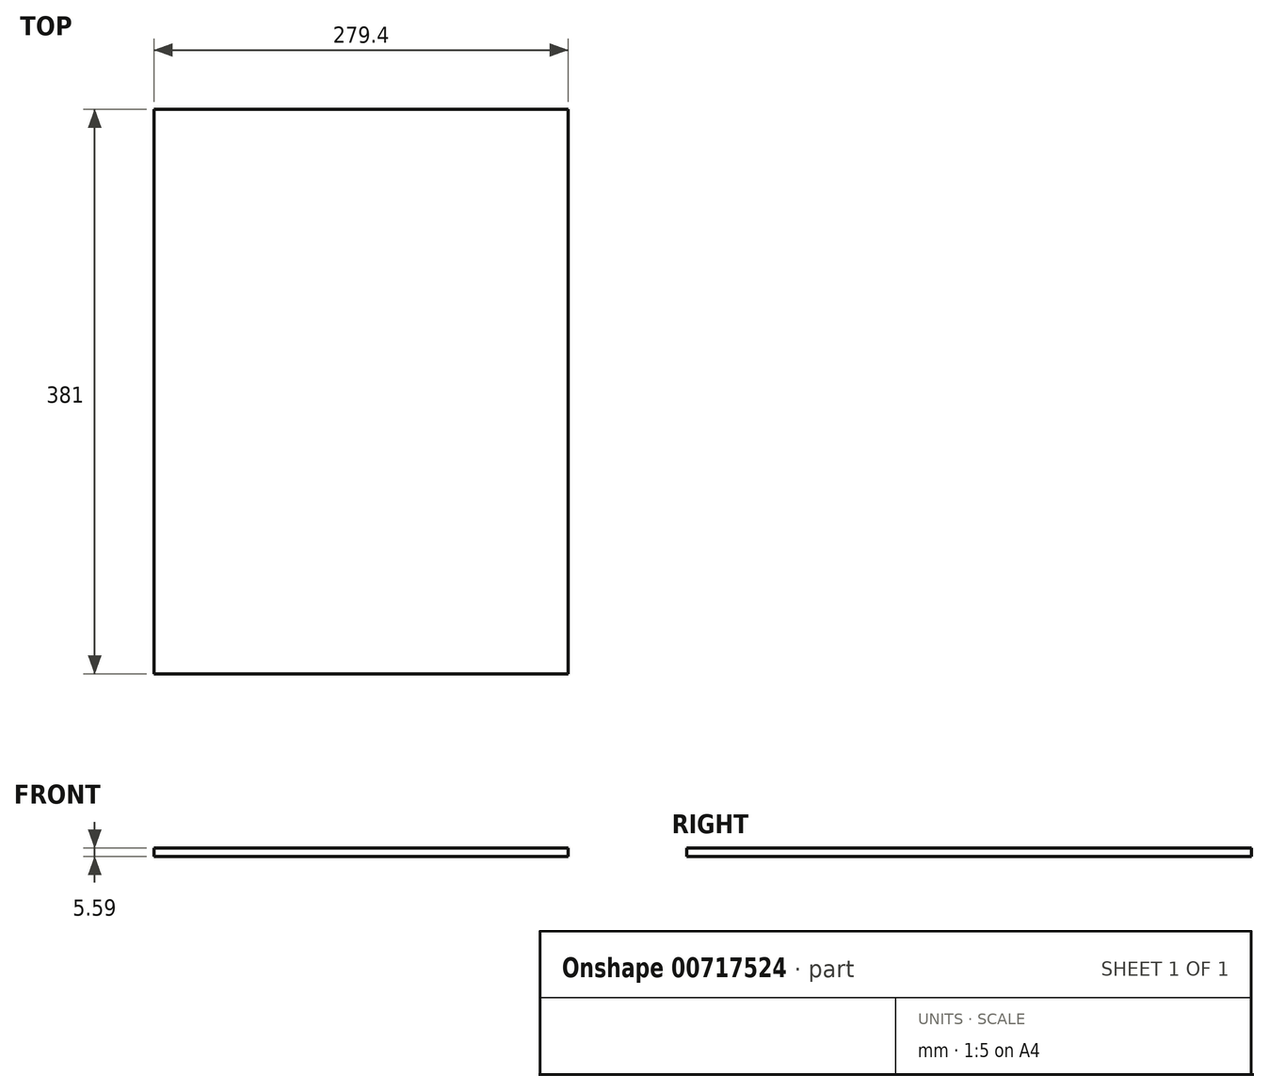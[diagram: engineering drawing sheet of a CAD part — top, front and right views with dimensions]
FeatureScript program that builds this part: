
annotation { "Feature Type Name" : "Feature", "Feature Type Description" : "" }
export const myFeature = defineFeature(function(context is Context, id is Id, definition is map)
    precondition{}
    {
        {
            var Q0;
            Q0=qCreatedBy(makeId("Top.planeOp"),FACE);
            var sketch = newSketch(context, id + "F0", { "sketchPlane" : qUnion([Q0])});
            skLineSegment(sketch, "E0.bottom", {"start": v(-139.7, 190.5) * mm, "end": v(139.7, 190.5) * mm});
            skLineSegment(sketch, "E0.top", {"start": v(-139.7, -190.5) * mm, "end": v(139.7, -190.5) * mm});
            skLineSegment(sketch, "E0.left", {"start": v(-139.7, 190.5) * mm, "end": v(-139.7, -190.5) * mm});
            skLineSegment(sketch, "E0.right", {"start": v(139.7, 190.5) * mm, "end": v(139.7, -190.5) * mm});
            skPoint(sketch, "E0.middle", {"position": v(0, 0) * mm});
            skSolve(sketch);
        }
        {
            var Q0;
            Q0=makeQuery(id+"F0.imprint","IMPRINT",FACE,{"disambiguationData":[TD([[makeQuery(id+"F0.imprint","IMPRINT",EDGE,{"derivedFrom":sQuery(id+"F0.wireOp",EDGE,"E0.bottom")}),-1.0]])]});
            extrude(context, id + "F1", {"entities" : qUnion([Q0]), "depth" : 5.6 * mm, "offsetDistance" : 25.4 * mm});
        }
    });
